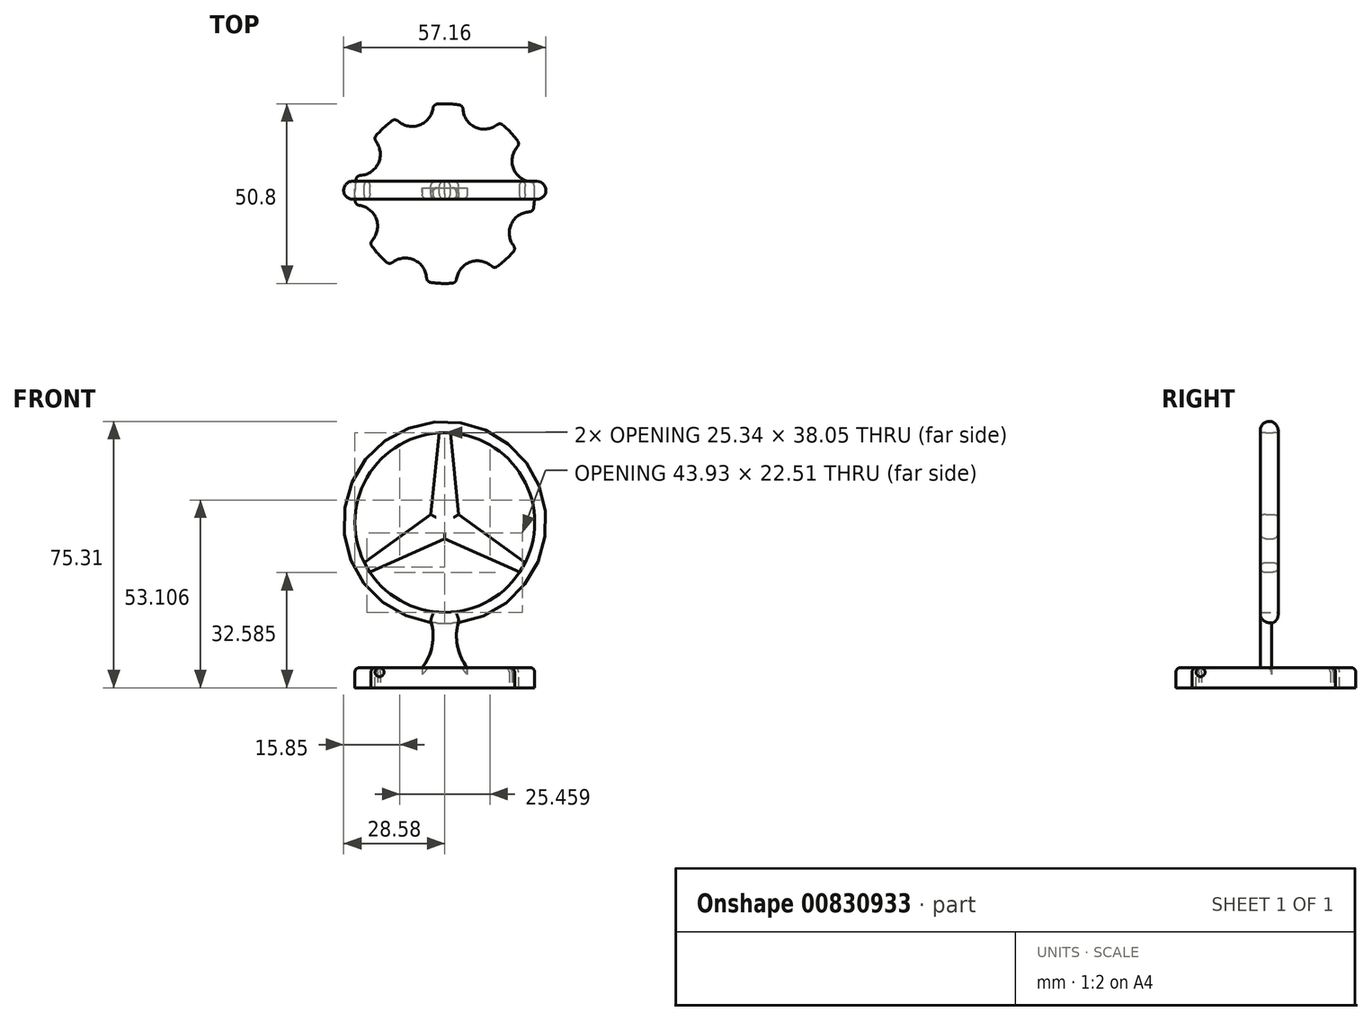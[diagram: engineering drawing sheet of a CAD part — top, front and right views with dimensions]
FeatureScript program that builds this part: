
annotation { "Feature Type Name" : "Feature", "Feature Type Description" : "" }
export const myFeature = defineFeature(function(context is Context, id is Id, definition is map)
    precondition{}
    {
        {
            var Q0;
            Q0=qCreatedBy(makeId("Front.planeOp"),FACE);
            var sketch = newSketch(context, id + "F0", { "sketchPlane" : qUnion([Q0])});
            skCircle(sketch, "E0", {"center": v(0, 0) * mm, "radius": 25.4 * mm});
            skCircle(sketch, "E1", {"center": v(0, 0) * mm, "radius": 28.58 * mm});
            skLineSegment(sketch, "E2", {"start": v(0, 0) * mm, "end": v(0, 28.58) * mm});
            skLineSegment(sketch, "E3", {"start": v(0, 0) * mm, "end": v(24.75, -14.29) * mm});
            skLineSegment(sketch, "E4", {"start": v(0, 0) * mm, "end": v(-24.75, -14.29) * mm});
            skPoint(sketch, "E5", {"position": v(-1.27, 28.55) * mm});
            skPoint(sketch, "E6.MirrorP", {"position": v(1.27, 28.55) * mm});
            skPoint(sketch, "E7.1.0", {"position": v(-24.09, -15.37) * mm});
            skPoint(sketch, "E7.1.1", {"position": v(-25.36, -13.17) * mm});
            skPoint(sketch, "E7.2.0", {"position": v(25.36, -13.17) * mm});
            skPoint(sketch, "E7.2.1", {"position": v(24.09, -15.37) * mm});
            skLineSegment(sketch, "E8", {"start": v(-1.27, 28.55) * mm, "end": v(-3.95, 2.28) * mm});
            skLineSegment(sketch, "E9", {"start": v(1.27, 28.55) * mm, "end": v(3.95, 2.28) * mm});
            skLineSegment(sketch, "E10", {"start": v(-3.95, 2.28) * mm, "end": v(-25.36, -13.17) * mm});
            skLineSegment(sketch, "E11", {"start": v(0, -4.56) * mm, "end": v(-24.09, -15.37) * mm});
            skLineSegment(sketch, "E12", {"start": v(0, -4.56) * mm, "end": v(24.09, -15.37) * mm});
            skLineSegment(sketch, "E13", {"start": v(3.95, 2.28) * mm, "end": v(25.36, -13.17) * mm});
            skSolve(sketch);
        }
        {
            var Q0;
            {var subQ1=sQuery(id+"F0.wireOp",EDGE,"E2");var subQ3=sQuery(id+"F0.wireOp",EDGE,"E0");var subQ4=makeQuery(id+"F0.imprint","INTERSECT",VERTEX,{"derivedFrom":[subQ3,subQ1]});Q0=makeQuery(id+"F0.imprint","IMPRINT",FACE,{"disambiguationData":[TD([[makeQuery(id+"F0.imprint","IMPRINT",EDGE,{"disambiguationData":[TD([[subQ4,1.0]])],"derivedFrom":subQ3}),1.0]])]});}
            var Q1;
            {var subQ3=sQuery(id+"F0.wireOp",EDGE,"E0");var subQ8=sQuery(id+"F0.wireOp",EDGE,"E2");var subQ10=makeQuery(id+"F0.imprint","INTERSECT",VERTEX,{"derivedFrom":[subQ3,subQ8]});Q1=makeQuery(id+"F0.imprint","IMPRINT",FACE,{"disambiguationData":[TD([[makeQuery(id+"F0.imprint","IMPRINT",EDGE,{"disambiguationData":[TD([[subQ10,-1.0]])],"derivedFrom":subQ3}),1.0]])]});}
            var Q2;
            {var subQ3=sQuery(id+"F0.wireOp",EDGE,"E0");var subQ5=sQuery(id+"F0.wireOp",EDGE,"E4");var subQ9=makeQuery(id+"F0.imprint","INTERSECT",VERTEX,{"derivedFrom":[subQ3,subQ5]});Q2=makeQuery(id+"F0.imprint","IMPRINT",FACE,{"disambiguationData":[TD([[makeQuery(id+"F0.imprint","IMPRINT",EDGE,{"disambiguationData":[TD([[subQ9,-1.0]])],"derivedFrom":subQ3}),1.0]])]});}
            extrude(context, id + "F1", {"entities" : qUnion([Q0, Q1, Q2]), "depth" : 5.08 * mm, "offsetDistance" : 25.4 * mm});
        }
        {
            var Q0;
            {var subQ0=sQuery(id+"F0.wireOp",EDGE,"ssB0D0hk-YjeL-rh0P-DfQI-fDgbEcnUojq0");var subQ1=sQuery(id+"F0.wireOp",EDGE,"E0");var subQ2=makeQuery(id+"F0.imprint","INTERSECT",VERTEX,{"derivedFrom":[subQ1,subQ0]});Q0=makeQuery(id+"F0.imprint","IMPRINT",FACE,{"disambiguationData":[TD([[makeQuery(id+"F0.imprint","IMPRINT",EDGE,{"disambiguationData":[TD([[subQ2,-1.0]])],"derivedFrom":subQ1}),-1.0]])]});}
            var Q1;
            {var subQ0=sQuery(id+"F0.wireOp",EDGE,"vXSUIzrc-3aUM-OjzA-1S35-c0gWzFx0R5wS");var subQ1=sQuery(id+"F0.wireOp",EDGE,"E0");var subQ2=makeQuery(id+"F0.imprint","INTERSECT",VERTEX,{"derivedFrom":[subQ1,subQ0]});Q1=makeQuery(id+"F0.imprint","IMPRINT",FACE,{"disambiguationData":[TD([[makeQuery(id+"F0.imprint","IMPRINT",EDGE,{"disambiguationData":[TD([[subQ2,-1.0]])],"derivedFrom":subQ1}),-1.0]])]});}
            var Q2;
            {var subQ0=sQuery(id+"F0.wireOp",EDGE,"Dz0Ez9dQ-trLA-jqhS-6Bqc-P0eBwSrEy02r");var subQ1=sQuery(id+"F0.wireOp",EDGE,"E0");var subQ2=makeQuery(id+"F0.imprint","INTERSECT",VERTEX,{"derivedFrom":[subQ1,subQ0]});Q2=makeQuery(id+"F0.imprint","IMPRINT",FACE,{"disambiguationData":[TD([[makeQuery(id+"F0.imprint","IMPRINT",EDGE,{"disambiguationData":[TD([[subQ2,-1.0]])],"derivedFrom":subQ1}),-1.0]])]});}
            var Q3;
            {var subQ0=sQuery(id+"F0.wireOp",EDGE,"E4");var subQ1=sQuery(id+"F0.wireOp",EDGE,"E0");var subQ2=makeQuery(id+"F0.imprint","INTERSECT",VERTEX,{"derivedFrom":[subQ1,subQ0]});Q3=makeQuery(id+"F0.imprint","IMPRINT",FACE,{"disambiguationData":[TD([[makeQuery(id+"F0.imprint","IMPRINT",EDGE,{"disambiguationData":[TD([[subQ2,-1.0]])],"derivedFrom":subQ1}),-1.0]])]});}
            var Q4;
            {var subQ0=sQuery(id+"F0.wireOp",EDGE,"6kq6KJOS-Uhyc-XBXJ-xyOy-W2txLPaZNpbT");var subQ1=sQuery(id+"F0.wireOp",EDGE,"E0");var subQ2=makeQuery(id+"F0.imprint","INTERSECT",VERTEX,{"derivedFrom":[subQ1,subQ0]});Q4=makeQuery(id+"F0.imprint","IMPRINT",FACE,{"disambiguationData":[TD([[makeQuery(id+"F0.imprint","IMPRINT",EDGE,{"disambiguationData":[TD([[subQ2,1.0]])],"derivedFrom":subQ1}),-1.0]])]});}
            var Q5;
            {var subQ0=sQuery(id+"F0.wireOp",EDGE,"O438YAgI-GwGk-3wlu-dIo6-Qv5mjCgu3Z9V");var subQ1=sQuery(id+"F0.wireOp",EDGE,"E0");var subQ2=makeQuery(id+"F0.imprint","INTERSECT",VERTEX,{"derivedFrom":[subQ1,subQ0]});Q5=makeQuery(id+"F0.imprint","IMPRINT",FACE,{"disambiguationData":[TD([[makeQuery(id+"F0.imprint","IMPRINT",EDGE,{"disambiguationData":[TD([[subQ2,-1.0]])],"derivedFrom":subQ1}),-1.0]])]});}
            var Q6;
            {var subQ0=sQuery(id+"F0.wireOp",EDGE,"E3");var subQ1=sQuery(id+"F0.wireOp",EDGE,"E0");var subQ2=makeQuery(id+"F0.imprint","INTERSECT",VERTEX,{"derivedFrom":[subQ1,subQ0]});Q6=makeQuery(id+"F0.imprint","IMPRINT",FACE,{"disambiguationData":[TD([[makeQuery(id+"F0.imprint","IMPRINT",EDGE,{"disambiguationData":[TD([[subQ2,-1.0]])],"derivedFrom":subQ1}),-1.0]])]});}
            var Q7;
            {var subQ0=sQuery(id+"F0.wireOp",EDGE,"E2");var subQ1=sQuery(id+"F0.wireOp",EDGE,"E0");var subQ2=makeQuery(id+"F0.imprint","INTERSECT",VERTEX,{"derivedFrom":[subQ1,subQ0]});Q7=makeQuery(id+"F0.imprint","IMPRINT",FACE,{"disambiguationData":[TD([[makeQuery(id+"F0.imprint","IMPRINT",EDGE,{"disambiguationData":[TD([[subQ2,-1.0]])],"derivedFrom":subQ1}),-1.0]])]});}
            var Q8;
            {var subQ0=sQuery(id+"F0.wireOp",EDGE,"E2");var subQ1=sQuery(id+"F0.wireOp",EDGE,"E0");var subQ2=makeQuery(id+"F0.imprint","INTERSECT",VERTEX,{"derivedFrom":[subQ1,subQ0]});Q8=makeQuery(id+"F0.imprint","IMPRINT",FACE,{"disambiguationData":[TD([[makeQuery(id+"F0.imprint","IMPRINT",EDGE,{"disambiguationData":[TD([[subQ2,1.0]])],"derivedFrom":subQ1}),-1.0]])]});}
            extrude(context, id + "F2", {"entities" : qUnion([Q0, Q1, Q2, Q3, Q4, Q5, Q6, Q7, Q8]), "operationType" : NewBodyOperationType.ADD, "depth" : 5.08 * mm, "offsetDistance" : 25.4 * mm});
        }
        {
            var Q0;
            {var subQ0=sQuery(id+"F0.wireOp",EDGE,"E0");Q0=makeQuery(id+"F2.boolean.opBoolean","MERGE",FACE,{"derivedFrom":[makeQuery(id+"F1.opExtrude","CAP_FACE",FACE,{"disambiguationData":[OSD([subQ0,sQuery(id+"F0.wireOp",EDGE,"6kq6KJOS-Uhyc-XBXJ-xyOy-W2txLPaZNpbT"),sQuery(id+"F0.wireOp",EDGE,"vXSUIzrc-3aUM-OjzA-1S35-c0gWzFx0R5wS"),sQuery(id+"F0.wireOp",EDGE,"jzs4yYJY-ds6L-RXk3-mSsh-zpbIfwapdUeN"),sQuery(id+"F0.wireOp",EDGE,"O438YAgI-GwGk-3wlu-dIo6-Qv5mjCgu3Z9V"),sQuery(id+"F0.wireOp",EDGE,"ssB0D0hk-YjeL-rh0P-DfQI-fDgbEcnUojq0"),sQuery(id+"F0.wireOp",EDGE,"Dz0Ez9dQ-trLA-jqhS-6Bqc-P0eBwSrEy02r")])],"isStart":false}),makeQuery(id+"F2.opExtrude","CAP_FACE",FACE,{"disambiguationData":[OSD([subQ0,sQuery(id+"F0.wireOp",EDGE,"E1")])],"isStart":false})]});}
            var sketch = newSketch(context, id + "F3", { "sketchPlane" : qUnion([Q0])});
            skArc(sketch, "E14", {"start": v(-6.35, -41.02) * mm, "mid": v(-3.59, -34.97) * mm, "end": v(-3.81, -28.32) * mm});
            skArc(sketch, "E15.MirrorCS", {"start": v(6.35, -41.02) * mm, "mid": v(3.59, -34.97) * mm, "end": v(3.81, -28.32) * mm});
            skLineSegment(sketch, "E16", {"start": v(-6.35, -41.02) * mm, "end": v(6.35, -41.02) * mm});
            skSolve(sketch);
        }
        {
            var Q0;
            {var subQ0=sQuery(id+"F3.wireOp",EDGE,"E14");Q0=makeQuery(id+"F3.imprint","IMPRINT",FACE,{"disambiguationData":[TD([[makeQuery(id+"F3.imprint","IMPRINT",EDGE,{"derivedFrom":subQ0}),-1.0]])]});}
            extrude(context, id + "F4", {"entities" : qUnion([Q0]), "operationType" : NewBodyOperationType.ADD, "oppositeDirection" : true, "depth" : 3.17 * mm, "offsetDistance" : 25.4 * mm});
        }
        {
            var Q0;
            Q0=makeQuery(id+"F4.opExtrude","SWEPT_FACE",FACE,{"disambiguationData":[OSD([sQuery(id+"F3.wireOp",EDGE,"E16")])]});
            var sketch = newSketch(context, id + "F5", { "sketchPlane" : qUnion([Q0])});
            skLineSegment(sketch, "E17", {"start": v(-1.27, 9.84) * mm, "end": v(1.27, 9.84) * mm});
            skLineSegment(sketch, "E18", {"start": v(-6.35, 3.5) * mm, "end": v(6.35, 3.5) * mm});
            skArc(sketch, "E19", {"start": v(-1.27, 9.84) * mm, "mid": v(-4.75, 8.47) * mm, "end": v(-6.35, 5.08) * mm});
            skArc(sketch, "E20", {"start": v(6.35, 5.08) * mm, "mid": v(4.75, 8.47) * mm, "end": v(1.27, 9.84) * mm});
            skArc(sketch, "E21.MirrorCS", {"start": v(6.35, 1.9) * mm, "mid": v(4.75, -1.48) * mm, "end": v(1.27, -2.86) * mm});
            skLineSegment(sketch, "E22.MirrorCS", {"start": v(-1.27, -2.86) * mm, "end": v(1.27, -2.86) * mm});
            skArc(sketch, "E23.MirrorCS", {"start": v(-1.27, -2.86) * mm, "mid": v(-4.75, -1.48) * mm, "end": v(-6.35, 1.9) * mm});
            skSolve(sketch);
        }
        {
            var Q0;
            Q0=makeQuery(id+"F5.imprint","IMPRINT",FACE,{"disambiguationData":[TD([[makeQuery(id+"F5.imprint","IMPRINT",EDGE,{"derivedFrom":sQuery(id+"F5.wireOp",EDGE,"E17")}),-1.0]])]});
            var Q1;
            {var subQ0=sQuery(id+"F5.wireOp",EDGE,"E18");Q1=makeQuery(id+"F5.imprint","IMPRINT",FACE,{"disambiguationData":[TD([[makeQuery(id+"F5.imprint","IMPRINT",EDGE,{"derivedFrom":subQ0}),1.0]])]});}
            var Q2;
            {var subQ0=sQuery(id+"F5.wireOp",EDGE,"E18");Q2=makeQuery(id+"F5.imprint","IMPRINT",FACE,{"disambiguationData":[TD([[makeQuery(id+"F5.imprint","IMPRINT",EDGE,{"derivedFrom":subQ0}),-1.0]])]});}
            var Q3;
            Q3=makeQuery(id+"F5.imprint","IMPRINT",FACE,{"disambiguationData":[TD([[makeQuery(id+"F5.imprint","IMPRINT",EDGE,{"derivedFrom":sQuery(id+"F5.wireOp",EDGE,"E21.MirrorCS")}),-1.0]])]});
            extrude(context, id + "F6", {"entities" : qUnion([Q0, Q1, Q2, Q3]), "operationType" : NewBodyOperationType.ADD, "depth" : 3.17 * mm, "offsetDistance" : 25.4 * mm});
        }
        {
            var Q0;
            Q0=makeQuery(id+"F2.opExtrude","CAP_EDGE",EDGE,{"disambiguationData":[OSD([sQuery(id+"F0.wireOp",EDGE,"E1")])],"isStart":false});
            var Q1;
            Q1=makeQuery(id+"F2.opExtrude","CAP_EDGE",EDGE,{"disambiguationData":[OSD([sQuery(id+"F0.wireOp",EDGE,"E1")])],"isStart":true});
            fillet(context, id + "F7", {"entities" : qUnion([Q0, Q1]), "radius" : 2.54 * mm, "tangentPropagation" : true, "allowEdgeOverflow" : false});
        }
        {
            var Q0;
            Q0=makeQuery(id+"F4.opExtrude","CAP_EDGE",EDGE,{"disambiguationData":[OSD([sQuery(id+"F3.wireOp",EDGE,"E15.MirrorCS")])],"isStart":false});
            var Q1;
            Q1=makeQuery(id+"F4.opExtrude","CAP_EDGE",EDGE,{"disambiguationData":[OSD([sQuery(id+"F3.wireOp",EDGE,"E14")])],"isStart":false});
            var Q2;
            Q2=makeQuery(id+"F4.opExtrude","CAP_EDGE",EDGE,{"disambiguationData":[OSD([sQuery(id+"F3.wireOp",EDGE,"E14")])],"isStart":true});
            var Q3;
            Q3=makeQuery(id+"F4.opExtrude","CAP_EDGE",EDGE,{"disambiguationData":[OSD([sQuery(id+"F3.wireOp",EDGE,"E15.MirrorCS")])],"isStart":true});
            fillet(context, id + "F8", {"entities" : qUnion([Q0, Q1, Q2, Q3]), "radius" : 1.27 * mm, "tangentPropagation" : true, "allowEdgeOverflow" : false});
        }
        {
            var Q0;
            Q0=makeQuery(id+"F6.opExtrude","CAP_FACE",FACE,{"disambiguationData":[OSD([sQuery(id+"F3.wireOp",EDGE,"E14"),sQuery(id+"F3.wireOp",EDGE,"E15.MirrorCS"),sQuery(id+"F3.wireOp",EDGE,"E16"),sQuery(id+"F5.wireOp",EDGE,"E17"),sQuery(id+"F5.wireOp",EDGE,"E19"),sQuery(id+"F5.wireOp",EDGE,"E20"),sQuery(id+"F5.wireOp",EDGE,"E21.MirrorCS"),sQuery(id+"F5.wireOp",EDGE,"E22.MirrorCS"),sQuery(id+"F5.wireOp",EDGE,"E23.MirrorCS")])],"isStart":false});
            var sketch = newSketch(context, id + "F9", { "sketchPlane" : qUnion([Q0])});
            skLineSegment(sketch, "E24", {"start": v(-6.35, 3.5) * mm, "end": v(6.35, 3.5) * mm});
            skLineSegment(sketch, "E25", {"start": v(0, 9.84) * mm, "end": v(0, -2.86) * mm});
            skCircle(sketch, "E26", {"center": v(0, 3.5) * mm, "radius": 25.4 * mm});
            skPoint(sketch, "E27.center", {"position": v(0, 0) * mm});
            skArc(sketch, "E28", {"start": v(-15.5, 23.61) * mm, "mid": v(-8.63, 22.26) * mm, "end": v(-5.18, 28.36) * mm});
            skArc(sketch, "E29.1.0", {"start": v(-25.19, 6.75) * mm, "mid": v(-19.37, 10.66) * mm, "end": v(-21.24, 17.41) * mm});
            skArc(sketch, "E29.2.0", {"start": v(-20.12, -12.01) * mm, "mid": v(-18.77, -5.14) * mm, "end": v(-24.87, -1.69) * mm});
            skArc(sketch, "E29.3.0", {"start": v(-3.26, -21.7) * mm, "mid": v(-7.17, -15.88) * mm, "end": v(-13.92, -17.75) * mm});
            skArc(sketch, "E29.4.0", {"start": v(15.5, -16.63) * mm, "mid": v(8.63, -15.27) * mm, "end": v(5.18, -21.37) * mm});
            skArc(sketch, "E29.5.0", {"start": v(25.19, 0.23) * mm, "mid": v(19.37, -3.68) * mm, "end": v(21.24, -10.43) * mm});
            skArc(sketch, "E29.6.0", {"start": v(20.12, 19) * mm, "mid": v(18.77, 12.12) * mm, "end": v(24.87, 8.67) * mm});
            skArc(sketch, "E29.7.0", {"start": v(3.26, 28.68) * mm, "mid": v(7.17, 22.86) * mm, "end": v(13.92, 24.74) * mm});
            skSolve(sketch);
        }
        {
            var Q0;
            {var subQ14=sQuery(id+"F9.wireOp",EDGE,"E28");Q0=makeQuery(id+"F9.imprint","IMPRINT",FACE,{"disambiguationData":[TD([[makeQuery(id+"F9.imprint","IMPRINT",EDGE,{"derivedFrom":subQ14}),-1.0]])]});}
            extrude(context, id + "F10", {"entities" : qUnion([Q0]), "oppositeDirection" : true, "depth" : 3.17 * mm, "offsetDistance" : 25.4 * mm});
        }
        {
            var Q0;
            Q0=makeQuery(id+"F10.opExtrude","SWEPT_BODY",BODY,{"disambiguationData":[OSD([sQuery(id+"F3.wireOp",EDGE,"E14"),sQuery(id+"F3.wireOp",EDGE,"E15.MirrorCS"),sQuery(id+"F3.wireOp",EDGE,"E16"),sQuery(id+"F5.wireOp",EDGE,"E17"),sQuery(id+"F5.wireOp",EDGE,"E19"),sQuery(id+"F5.wireOp",EDGE,"E20"),sQuery(id+"F5.wireOp",EDGE,"E21.MirrorCS"),sQuery(id+"F5.wireOp",EDGE,"E22.MirrorCS"),sQuery(id+"F5.wireOp",EDGE,"E23.MirrorCS"),sQuery(id+"F9.wireOp",EDGE,"E26"),sQuery(id+"F9.wireOp",EDGE,"E28"),sQuery(id+"F9.wireOp",EDGE,"E29.1.0"),sQuery(id+"F9.wireOp",EDGE,"E29.2.0"),sQuery(id+"F9.wireOp",EDGE,"E29.3.0"),sQuery(id+"F9.wireOp",EDGE,"E29.4.0"),sQuery(id+"F9.wireOp",EDGE,"E29.5.0"),sQuery(id+"F9.wireOp",EDGE,"E29.6.0"),sQuery(id+"F9.wireOp",EDGE,"E29.7.0")])]});
            var Q1;
            Q1=makeQuery(id+"F1.opExtrude","SWEPT_BODY",BODY,{"disambiguationData":[OSD([sQuery(id+"F0.wireOp",EDGE,"E0"),sQuery(id+"F0.wireOp",EDGE,"6kq6KJOS-Uhyc-XBXJ-xyOy-W2txLPaZNpbT"),sQuery(id+"F0.wireOp",EDGE,"vXSUIzrc-3aUM-OjzA-1S35-c0gWzFx0R5wS"),sQuery(id+"F0.wireOp",EDGE,"jzs4yYJY-ds6L-RXk3-mSsh-zpbIfwapdUeN"),sQuery(id+"F0.wireOp",EDGE,"O438YAgI-GwGk-3wlu-dIo6-Qv5mjCgu3Z9V"),sQuery(id+"F0.wireOp",EDGE,"ssB0D0hk-YjeL-rh0P-DfQI-fDgbEcnUojq0"),sQuery(id+"F0.wireOp",EDGE,"Dz0Ez9dQ-trLA-jqhS-6Bqc-P0eBwSrEy02r")])]});
            var Q2;
            Q2=makeQuery(id+"F10.opExtrude","CAP_FACE",FACE,{"disambiguationData":[OSD([sQuery(id+"F3.wireOp",EDGE,"E14"),sQuery(id+"F3.wireOp",EDGE,"E15.MirrorCS"),sQuery(id+"F3.wireOp",EDGE,"E16"),sQuery(id+"F5.wireOp",EDGE,"E17"),sQuery(id+"F5.wireOp",EDGE,"E19"),sQuery(id+"F5.wireOp",EDGE,"E20"),sQuery(id+"F5.wireOp",EDGE,"E21.MirrorCS"),sQuery(id+"F5.wireOp",EDGE,"E22.MirrorCS"),sQuery(id+"F5.wireOp",EDGE,"E23.MirrorCS"),sQuery(id+"F9.wireOp",EDGE,"E26"),sQuery(id+"F9.wireOp",EDGE,"E28"),sQuery(id+"F9.wireOp",EDGE,"E29.1.0"),sQuery(id+"F9.wireOp",EDGE,"E29.2.0"),sQuery(id+"F9.wireOp",EDGE,"E29.3.0"),sQuery(id+"F9.wireOp",EDGE,"E29.4.0"),sQuery(id+"F9.wireOp",EDGE,"E29.5.0"),sQuery(id+"F9.wireOp",EDGE,"E29.6.0"),sQuery(id+"F9.wireOp",EDGE,"E29.7.0")])],"isStart":false});
            booleanBodies(context, id + "F11", {"operationType" : BooleanOperationType.SUBTRACTION, "tools" : qUnion([Q0]), "targets" : qUnion([Q1]), "offset" : true, "entitiesToOffset" : qUnion([Q2]), "offsetDistance" : 2.54 * mm, "keepTools" : true});
        }
        {
            var Q0;
            Q0=makeQuery(id+"F10.opExtrude","CAP_EDGE",EDGE,{"disambiguationData":[OSD([sQuery(id+"F9.wireOp",EDGE,"E29.6.0")])],"isStart":false});
            var Q1;
            {var subQ0=sQuery(id+"F9.wireOp",EDGE,"E26");Q1=makeQuery(id+"F10.opExtrude","CAP_EDGE",EDGE,{"disambiguationData":[OSD([subQ0]),TDD([makeQuery(id+"F9.imprint","IMPRINT",EDGE,{"disambiguationData":[TD([[makeQuery(id+"F9.imprint","INTERSECT",VERTEX,{"disambiguationData":[OD(0.0)],"derivedFrom":[subQ0,sQuery(id+"F9.wireOp",EDGE,"E29.6.0")]}),-1.0]])],"derivedFrom":subQ0})])],"isStart":false});}
            var Q2;
            {var subQ0=sQuery(id+"F9.wireOp",EDGE,"E26");Q2=makeQuery(id+"F10.opExtrude","CAP_EDGE",EDGE,{"disambiguationData":[OSD([subQ0]),TDD([makeQuery(id+"F9.imprint","IMPRINT",EDGE,{"disambiguationData":[TD([[makeQuery(id+"F9.imprint","INTERSECT",VERTEX,{"disambiguationData":[OD(1.0)],"derivedFrom":[subQ0,sQuery(id+"F9.wireOp",EDGE,"E28")]}),1.0]])],"derivedFrom":subQ0})])],"isStart":false});}
            var Q3;
            Q3=makeQuery(id+"F10.opExtrude","CAP_EDGE",EDGE,{"disambiguationData":[OSD([sQuery(id+"F9.wireOp",EDGE,"E29.7.0")])],"isStart":false});
            var Q4;
            Q4=makeQuery(id+"F10.opExtrude","CAP_EDGE",EDGE,{"disambiguationData":[OSD([sQuery(id+"F9.wireOp",EDGE,"E28")])],"isStart":false});
            var Q5;
            {var subQ0=sQuery(id+"F9.wireOp",EDGE,"E26");Q5=makeQuery(id+"F10.opExtrude","CAP_EDGE",EDGE,{"disambiguationData":[OSD([subQ0]),TDD([makeQuery(id+"F9.imprint","IMPRINT",EDGE,{"disambiguationData":[TD([[makeQuery(id+"F9.imprint","INTERSECT",VERTEX,{"disambiguationData":[OD(0.0)],"derivedFrom":[subQ0,sQuery(id+"F9.wireOp",EDGE,"E28")]}),-1.0]])],"derivedFrom":subQ0})])],"isStart":false});}
            var Q6;
            Q6=makeQuery(id+"F10.opExtrude","CAP_EDGE",EDGE,{"disambiguationData":[OSD([sQuery(id+"F9.wireOp",EDGE,"E29.1.0")])],"isStart":false});
            var Q7;
            {var subQ0=sQuery(id+"F9.wireOp",EDGE,"E26");Q7=makeQuery(id+"F10.opExtrude","CAP_EDGE",EDGE,{"disambiguationData":[OSD([subQ0]),TDD([makeQuery(id+"F9.imprint","IMPRINT",EDGE,{"disambiguationData":[TD([[makeQuery(id+"F9.imprint","INTERSECT",VERTEX,{"disambiguationData":[OD(0.0)],"derivedFrom":[subQ0,sQuery(id+"F9.wireOp",EDGE,"E29.1.0")]}),-1.0]])],"derivedFrom":subQ0})])],"isStart":false});}
            var Q8;
            Q8=makeQuery(id+"F10.opExtrude","CAP_EDGE",EDGE,{"disambiguationData":[OSD([sQuery(id+"F9.wireOp",EDGE,"E29.2.0")])],"isStart":false});
            var Q9;
            {var subQ0=sQuery(id+"F9.wireOp",EDGE,"E26");Q9=makeQuery(id+"F10.opExtrude","CAP_EDGE",EDGE,{"disambiguationData":[OSD([subQ0]),TDD([makeQuery(id+"F9.imprint","IMPRINT",EDGE,{"disambiguationData":[TD([[makeQuery(id+"F9.imprint","INTERSECT",VERTEX,{"disambiguationData":[OD(0.0)],"derivedFrom":[subQ0,sQuery(id+"F9.wireOp",EDGE,"E29.2.0")]}),-1.0]])],"derivedFrom":subQ0})])],"isStart":false});}
            var Q10;
            Q10=makeQuery(id+"F10.opExtrude","CAP_EDGE",EDGE,{"disambiguationData":[OSD([sQuery(id+"F9.wireOp",EDGE,"E29.3.0")])],"isStart":false});
            var Q11;
            Q11=makeQuery(id+"F10.opExtrude","CAP_EDGE",EDGE,{"disambiguationData":[OSD([sQuery(id+"F9.wireOp",EDGE,"E29.4.0")])],"isStart":false});
            var Q12;
            Q12=makeQuery(id+"F10.opExtrude","CAP_EDGE",EDGE,{"disambiguationData":[OSD([sQuery(id+"F9.wireOp",EDGE,"E29.5.0")])],"isStart":false});
            var Q13;
            {var subQ0=sQuery(id+"F9.wireOp",EDGE,"E26");Q13=makeQuery(id+"F10.opExtrude","CAP_EDGE",EDGE,{"disambiguationData":[OSD([subQ0]),TDD([makeQuery(id+"F9.imprint","IMPRINT",EDGE,{"disambiguationData":[TD([[makeQuery(id+"F9.imprint","INTERSECT",VERTEX,{"disambiguationData":[OD(0.0)],"derivedFrom":[subQ0,sQuery(id+"F9.wireOp",EDGE,"E29.5.0")]}),-1.0]])],"derivedFrom":subQ0})])],"isStart":false});}
            var Q14;
            {var subQ0=sQuery(id+"F9.wireOp",EDGE,"E26");Q14=makeQuery(id+"F10.opExtrude","CAP_EDGE",EDGE,{"disambiguationData":[OSD([subQ0]),TDD([makeQuery(id+"F9.imprint","IMPRINT",EDGE,{"disambiguationData":[TD([[makeQuery(id+"F9.imprint","INTERSECT",VERTEX,{"disambiguationData":[OD(0.0)],"derivedFrom":[subQ0,sQuery(id+"F9.wireOp",EDGE,"E29.4.0")]}),-1.0]])],"derivedFrom":subQ0})])],"isStart":false});}
            var Q15;
            {var subQ0=sQuery(id+"F9.wireOp",EDGE,"E26");Q15=makeQuery(id+"F10.opExtrude","CAP_EDGE",EDGE,{"disambiguationData":[OSD([subQ0]),TDD([makeQuery(id+"F9.imprint","IMPRINT",EDGE,{"disambiguationData":[TD([[makeQuery(id+"F9.imprint","INTERSECT",VERTEX,{"disambiguationData":[OD(0.0)],"derivedFrom":[subQ0,sQuery(id+"F9.wireOp",EDGE,"E29.3.0")]}),-1.0]])],"derivedFrom":subQ0})])],"isStart":false});}
            var Q16;
            {var subQ0=sQuery(id+"F9.wireOp",EDGE,"E28");var subQ1=sQuery(id+"F9.wireOp",EDGE,"E26");Q16=makeQuery(id+"F10.opExtrude","SWEPT_EDGE",EDGE,{"disambiguationData":[OSD([subQ1,subQ0]),TDD([makeQuery(id+"F9.imprint","INTERSECT",VERTEX,{"disambiguationData":[OD(0.0)],"derivedFrom":[subQ1,subQ0]})])]});}
            var Q17;
            {var subQ0=sQuery(id+"F9.wireOp",EDGE,"E28");var subQ1=sQuery(id+"F9.wireOp",EDGE,"E26");Q17=makeQuery(id+"F10.opExtrude","SWEPT_EDGE",EDGE,{"disambiguationData":[OSD([subQ1,subQ0]),TDD([makeQuery(id+"F9.imprint","INTERSECT",VERTEX,{"disambiguationData":[OD(1.0)],"derivedFrom":[subQ1,subQ0]})])]});}
            var Q18;
            {var subQ0=sQuery(id+"F9.wireOp",EDGE,"E29.7.0");var subQ1=sQuery(id+"F9.wireOp",EDGE,"E26");Q18=makeQuery(id+"F10.opExtrude","SWEPT_EDGE",EDGE,{"disambiguationData":[OSD([subQ1,subQ0]),TDD([makeQuery(id+"F9.imprint","INTERSECT",VERTEX,{"disambiguationData":[OD(0.0)],"derivedFrom":[subQ1,subQ0]})])]});}
            var Q19;
            {var subQ0=sQuery(id+"F9.wireOp",EDGE,"E29.1.0");var subQ1=sQuery(id+"F9.wireOp",EDGE,"E26");Q19=makeQuery(id+"F10.opExtrude","SWEPT_EDGE",EDGE,{"disambiguationData":[OSD([subQ1,subQ0]),TDD([makeQuery(id+"F9.imprint","INTERSECT",VERTEX,{"disambiguationData":[OD(1.0)],"derivedFrom":[subQ1,subQ0]})])]});}
            var Q20;
            {var subQ0=sQuery(id+"F9.wireOp",EDGE,"E29.7.0");var subQ1=sQuery(id+"F9.wireOp",EDGE,"E26");Q20=makeQuery(id+"F10.opExtrude","SWEPT_EDGE",EDGE,{"disambiguationData":[OSD([subQ1,subQ0]),TDD([makeQuery(id+"F9.imprint","INTERSECT",VERTEX,{"disambiguationData":[OD(1.0)],"derivedFrom":[subQ1,subQ0]})])]});}
            var Q21;
            {var subQ0=sQuery(id+"F9.wireOp",EDGE,"E29.6.0");var subQ1=sQuery(id+"F9.wireOp",EDGE,"E26");Q21=makeQuery(id+"F10.opExtrude","SWEPT_EDGE",EDGE,{"disambiguationData":[OSD([subQ1,subQ0]),TDD([makeQuery(id+"F9.imprint","INTERSECT",VERTEX,{"disambiguationData":[OD(0.0)],"derivedFrom":[subQ1,subQ0]})])]});}
            var Q22;
            {var subQ0=sQuery(id+"F9.wireOp",EDGE,"E29.6.0");var subQ1=sQuery(id+"F9.wireOp",EDGE,"E26");Q22=makeQuery(id+"F10.opExtrude","SWEPT_EDGE",EDGE,{"disambiguationData":[OSD([subQ1,subQ0]),TDD([makeQuery(id+"F9.imprint","INTERSECT",VERTEX,{"disambiguationData":[OD(1.0)],"derivedFrom":[subQ1,subQ0]})])]});}
            var Q23;
            {var subQ0=sQuery(id+"F9.wireOp",EDGE,"E29.5.0");var subQ1=sQuery(id+"F9.wireOp",EDGE,"E26");Q23=makeQuery(id+"F10.opExtrude","SWEPT_EDGE",EDGE,{"disambiguationData":[OSD([subQ1,subQ0]),TDD([makeQuery(id+"F9.imprint","INTERSECT",VERTEX,{"disambiguationData":[OD(0.0)],"derivedFrom":[subQ1,subQ0]})])]});}
            var Q24;
            {var subQ0=sQuery(id+"F9.wireOp",EDGE,"E29.4.0");var subQ1=sQuery(id+"F9.wireOp",EDGE,"E26");Q24=makeQuery(id+"F10.opExtrude","SWEPT_EDGE",EDGE,{"disambiguationData":[OSD([subQ1,subQ0]),TDD([makeQuery(id+"F9.imprint","INTERSECT",VERTEX,{"disambiguationData":[OD(0.0)],"derivedFrom":[subQ1,subQ0]})])]});}
            var Q25;
            {var subQ0=sQuery(id+"F9.wireOp",EDGE,"E29.5.0");var subQ1=sQuery(id+"F9.wireOp",EDGE,"E26");Q25=makeQuery(id+"F10.opExtrude","SWEPT_EDGE",EDGE,{"disambiguationData":[OSD([subQ1,subQ0]),TDD([makeQuery(id+"F9.imprint","INTERSECT",VERTEX,{"disambiguationData":[OD(1.0)],"derivedFrom":[subQ1,subQ0]})])]});}
            var Q26;
            {var subQ0=sQuery(id+"F9.wireOp",EDGE,"E29.4.0");var subQ1=sQuery(id+"F9.wireOp",EDGE,"E26");Q26=makeQuery(id+"F10.opExtrude","SWEPT_EDGE",EDGE,{"disambiguationData":[OSD([subQ1,subQ0]),TDD([makeQuery(id+"F9.imprint","INTERSECT",VERTEX,{"disambiguationData":[OD(1.0)],"derivedFrom":[subQ1,subQ0]})])]});}
            var Q27;
            {var subQ0=sQuery(id+"F9.wireOp",EDGE,"E29.3.0");var subQ1=sQuery(id+"F9.wireOp",EDGE,"E26");Q27=makeQuery(id+"F10.opExtrude","SWEPT_EDGE",EDGE,{"disambiguationData":[OSD([subQ1,subQ0]),TDD([makeQuery(id+"F9.imprint","INTERSECT",VERTEX,{"disambiguationData":[OD(0.0)],"derivedFrom":[subQ1,subQ0]})])]});}
            var Q28;
            {var subQ0=sQuery(id+"F9.wireOp",EDGE,"E29.3.0");var subQ1=sQuery(id+"F9.wireOp",EDGE,"E26");Q28=makeQuery(id+"F10.opExtrude","SWEPT_EDGE",EDGE,{"disambiguationData":[OSD([subQ1,subQ0]),TDD([makeQuery(id+"F9.imprint","INTERSECT",VERTEX,{"disambiguationData":[OD(1.0)],"derivedFrom":[subQ1,subQ0]})])]});}
            var Q29;
            {var subQ0=sQuery(id+"F9.wireOp",EDGE,"E29.2.0");var subQ1=sQuery(id+"F9.wireOp",EDGE,"E26");Q29=makeQuery(id+"F10.opExtrude","SWEPT_EDGE",EDGE,{"disambiguationData":[OSD([subQ1,subQ0]),TDD([makeQuery(id+"F9.imprint","INTERSECT",VERTEX,{"disambiguationData":[OD(0.0)],"derivedFrom":[subQ1,subQ0]})])]});}
            var Q30;
            {var subQ0=sQuery(id+"F9.wireOp",EDGE,"E29.1.0");var subQ1=sQuery(id+"F9.wireOp",EDGE,"E26");Q30=makeQuery(id+"F10.opExtrude","SWEPT_EDGE",EDGE,{"disambiguationData":[OSD([subQ1,subQ0]),TDD([makeQuery(id+"F9.imprint","INTERSECT",VERTEX,{"disambiguationData":[OD(0.0)],"derivedFrom":[subQ1,subQ0]})])]});}
            var Q31;
            {var subQ0=sQuery(id+"F9.wireOp",EDGE,"E29.2.0");var subQ1=sQuery(id+"F9.wireOp",EDGE,"E26");Q31=makeQuery(id+"F10.opExtrude","SWEPT_EDGE",EDGE,{"disambiguationData":[OSD([subQ1,subQ0]),TDD([makeQuery(id+"F9.imprint","INTERSECT",VERTEX,{"disambiguationData":[OD(1.0)],"derivedFrom":[subQ1,subQ0]})])]});}
            fillet(context, id + "F12", {"entities" : qUnion([Q0, Q1, Q2, Q3, Q4, Q5, Q6, Q7, Q8, Q9, Q10, Q11, Q12, Q13, Q14, Q15, Q16, Q17, Q18, Q19, Q20, Q21, Q22, Q23, Q24, Q25, Q26, Q27, Q28, Q29, Q30, Q31]), "radius" : 1.27 * mm, "tangentPropagation" : true, "allowEdgeOverflow" : false});
        }
        {
            var Q0;
            Q0=makeQuery(id+"F10.opExtrude","CAP_FACE",FACE,{"disambiguationData":[OSD([sQuery(id+"F3.wireOp",EDGE,"E14"),sQuery(id+"F3.wireOp",EDGE,"E15.MirrorCS"),sQuery(id+"F3.wireOp",EDGE,"E16"),sQuery(id+"F5.wireOp",EDGE,"E17"),sQuery(id+"F5.wireOp",EDGE,"E19"),sQuery(id+"F5.wireOp",EDGE,"E20"),sQuery(id+"F5.wireOp",EDGE,"E21.MirrorCS"),sQuery(id+"F5.wireOp",EDGE,"E22.MirrorCS"),sQuery(id+"F5.wireOp",EDGE,"E23.MirrorCS"),sQuery(id+"F9.wireOp",EDGE,"E26"),sQuery(id+"F9.wireOp",EDGE,"E28"),sQuery(id+"F9.wireOp",EDGE,"E29.1.0"),sQuery(id+"F9.wireOp",EDGE,"E29.2.0"),sQuery(id+"F9.wireOp",EDGE,"E29.3.0"),sQuery(id+"F9.wireOp",EDGE,"E29.4.0"),sQuery(id+"F9.wireOp",EDGE,"E29.5.0"),sQuery(id+"F9.wireOp",EDGE,"E29.6.0"),sQuery(id+"F9.wireOp",EDGE,"E29.7.0")])],"isStart":true});
            extrude(context, id + "F13", {"entities" : qUnion([Q0]), "operationType" : NewBodyOperationType.ADD, "depth" : 2.54 * mm, "offsetDistance" : 25.4 * mm});
        }
        {
            var Q0;
            Q0=makeQuery(id+"F13.opExtrude","CAP_FACE",FACE,{"disambiguationData":[OSD([sQuery(id+"F3.wireOp",EDGE,"E14"),sQuery(id+"F3.wireOp",EDGE,"E15.MirrorCS"),sQuery(id+"F3.wireOp",EDGE,"E16"),sQuery(id+"F5.wireOp",EDGE,"E17"),sQuery(id+"F5.wireOp",EDGE,"E19"),sQuery(id+"F5.wireOp",EDGE,"E20"),sQuery(id+"F5.wireOp",EDGE,"E21.MirrorCS"),sQuery(id+"F5.wireOp",EDGE,"E22.MirrorCS"),sQuery(id+"F5.wireOp",EDGE,"E23.MirrorCS"),sQuery(id+"F9.wireOp",EDGE,"E26"),sQuery(id+"F9.wireOp",EDGE,"E28"),sQuery(id+"F9.wireOp",EDGE,"E29.1.0"),sQuery(id+"F9.wireOp",EDGE,"E29.2.0"),sQuery(id+"F9.wireOp",EDGE,"E29.3.0"),sQuery(id+"F9.wireOp",EDGE,"E29.4.0"),sQuery(id+"F9.wireOp",EDGE,"E29.5.0"),sQuery(id+"F9.wireOp",EDGE,"E29.6.0"),sQuery(id+"F9.wireOp",EDGE,"E29.7.0")])],"isStart":false});
            var sketch = newSketch(context, id + "F14", { "sketchPlane" : qUnion([Q0])});
            skLineSegment(sketch, "E30", {"start": v(-1.27, 9.84) * mm, "end": v(1.27, 9.84) * mm});
            skLineSegment(sketch, "E31", {"start": v(-1.27, -2.86) * mm, "end": v(1.27, -2.86) * mm});
            skLineSegment(sketch, "E32", {"start": v(-6.35, 5.08) * mm, "end": v(-6.35, 1.9) * mm});
            skLineSegment(sketch, "E33", {"start": v(6.35, 5.08) * mm, "end": v(6.35, 1.9) * mm});
            skArc(sketch, "E34", {"start": v(-1.27, 9.84) * mm, "mid": v(-4.75, 8.47) * mm, "end": v(-6.35, 5.08) * mm});
            skArc(sketch, "E35", {"start": v(6.35, 5.08) * mm, "mid": v(4.75, 8.47) * mm, "end": v(1.27, 9.84) * mm});
            skArc(sketch, "E36", {"start": v(-6.35, 1.9) * mm, "mid": v(-4.75, -1.48) * mm, "end": v(-1.27, -2.86) * mm});
            skArc(sketch, "E37", {"start": v(1.27, -2.86) * mm, "mid": v(4.75, -1.48) * mm, "end": v(6.35, 1.9) * mm});
            skSolve(sketch);
        }
        {
            var Q0;
            Q0 = qSketchRegion(id + "F14", true);
            extrude(context, id + "F15", {"entities" : qUnion([Q0]), "operationType" : NewBodyOperationType.ADD, "oppositeDirection" : true, "depth" : 2.54 * mm, "offsetDistance" : 25.4 * mm});
        }
        {
            var Q0;
            Q0=makeQuery(id+"F1.opExtrude","CAP_EDGE",EDGE,{"disambiguationData":[OSD([sQuery(id+"F0.wireOp",EDGE,"E9")])],"isStart":false});
            var Q1;
            Q1=makeQuery(id+"F1.opExtrude","CAP_EDGE",EDGE,{"disambiguationData":[OSD([sQuery(id+"F0.wireOp",EDGE,"E8")])],"isStart":false});
            var Q2;
            Q2=makeQuery(id+"F1.opExtrude","CAP_EDGE",EDGE,{"disambiguationData":[OSD([sQuery(id+"F0.wireOp",EDGE,"E13")])],"isStart":false});
            var Q3;
            Q3=makeQuery(id+"F1.opExtrude","CAP_EDGE",EDGE,{"disambiguationData":[OSD([sQuery(id+"F0.wireOp",EDGE,"E10")])],"isStart":false});
            var Q4;
            Q4=makeQuery(id+"F1.opExtrude","CAP_EDGE",EDGE,{"disambiguationData":[OSD([sQuery(id+"F0.wireOp",EDGE,"E11")])],"isStart":false});
            var Q5;
            Q5=makeQuery(id+"F1.opExtrude","CAP_EDGE",EDGE,{"disambiguationData":[OSD([sQuery(id+"F0.wireOp",EDGE,"E12")])],"isStart":false});
            var Q6;
            Q6=makeQuery(id+"F1.opExtrude","CAP_EDGE",EDGE,{"disambiguationData":[OSD([sQuery(id+"F0.wireOp",EDGE,"E9")])],"isStart":true});
            var Q7;
            Q7=makeQuery(id+"F1.opExtrude","CAP_EDGE",EDGE,{"disambiguationData":[OSD([sQuery(id+"F0.wireOp",EDGE,"E8")])],"isStart":true});
            var Q8;
            Q8=makeQuery(id+"F1.opExtrude","CAP_EDGE",EDGE,{"disambiguationData":[OSD([sQuery(id+"F0.wireOp",EDGE,"E13")])],"isStart":true});
            var Q9;
            Q9=makeQuery(id+"F1.opExtrude","CAP_EDGE",EDGE,{"disambiguationData":[OSD([sQuery(id+"F0.wireOp",EDGE,"E11")])],"isStart":true});
            var Q10;
            Q10=makeQuery(id+"F1.opExtrude","CAP_EDGE",EDGE,{"disambiguationData":[OSD([sQuery(id+"F0.wireOp",EDGE,"E10")])],"isStart":true});
            var Q11;
            Q11=makeQuery(id+"F1.opExtrude","CAP_EDGE",EDGE,{"disambiguationData":[OSD([sQuery(id+"F0.wireOp",EDGE,"E12")])],"isStart":true});
            fillet(context, id + "F16", {"entities" : qUnion([Q0, Q1, Q2, Q3, Q4, Q5, Q6, Q7, Q8, Q9, Q10, Q11]), "radius" : 1.52 * mm, "tangentPropagation" : true, "allowEdgeOverflow" : false});
        }
    });
